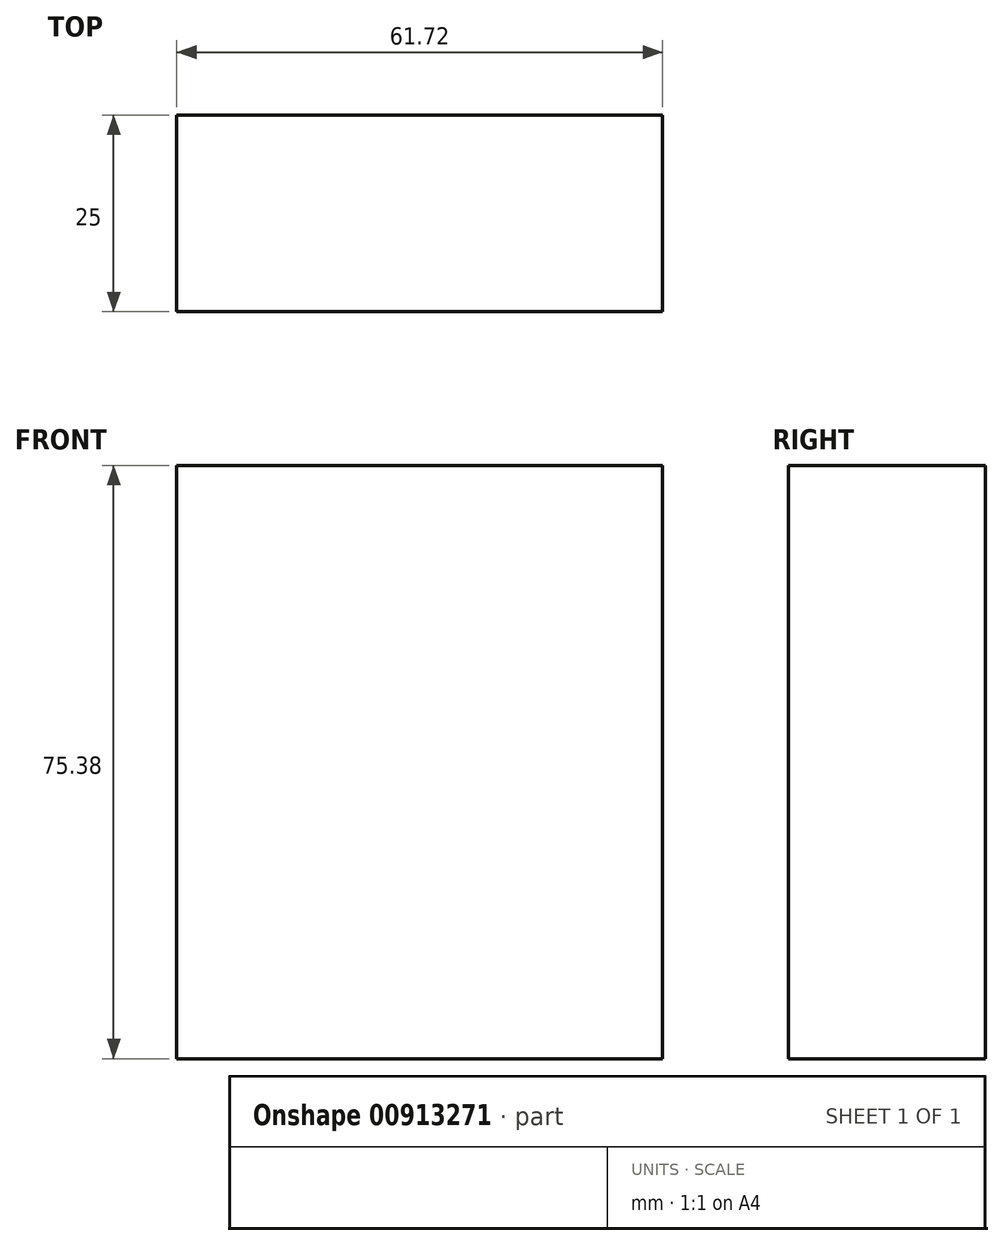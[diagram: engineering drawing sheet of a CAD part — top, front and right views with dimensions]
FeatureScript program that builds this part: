
annotation { "Feature Type Name" : "Feature", "Feature Type Description" : "" }
export const myFeature = defineFeature(function(context is Context, id is Id, definition is map)
    precondition{}
    {
        {
            var Q0;
            Q0=qCreatedBy(makeId("Front.planeOp"),FACE);
            var sketch = newSketch(context, id + "F0", { "sketchPlane" : qUnion([Q0])});
            skLineSegment(sketch, "E0.bottom", {"start": v(30.86, -37.7) * mm, "end": v(-30.86, -37.7) * mm});
            skLineSegment(sketch, "E0.top", {"start": v(30.86, 37.7) * mm, "end": v(-30.86, 37.7) * mm});
            skLineSegment(sketch, "E0.left", {"start": v(30.86, -37.7) * mm, "end": v(30.86, 37.7) * mm});
            skLineSegment(sketch, "E0.right", {"start": v(-30.86, -37.7) * mm, "end": v(-30.86, 37.7) * mm});
            skPoint(sketch, "E0.middle", {"position": v(0, 0) * mm});
            skSolve(sketch);
        }
        {
            var Q0;
            Q0 = qSketchRegion(id + "F0", true);
            extrude(context, id + "F1", {"entities" : qUnion([Q0]), "depth" : 25 * mm, "offsetDistance" : 25 * mm});
        }
    });
